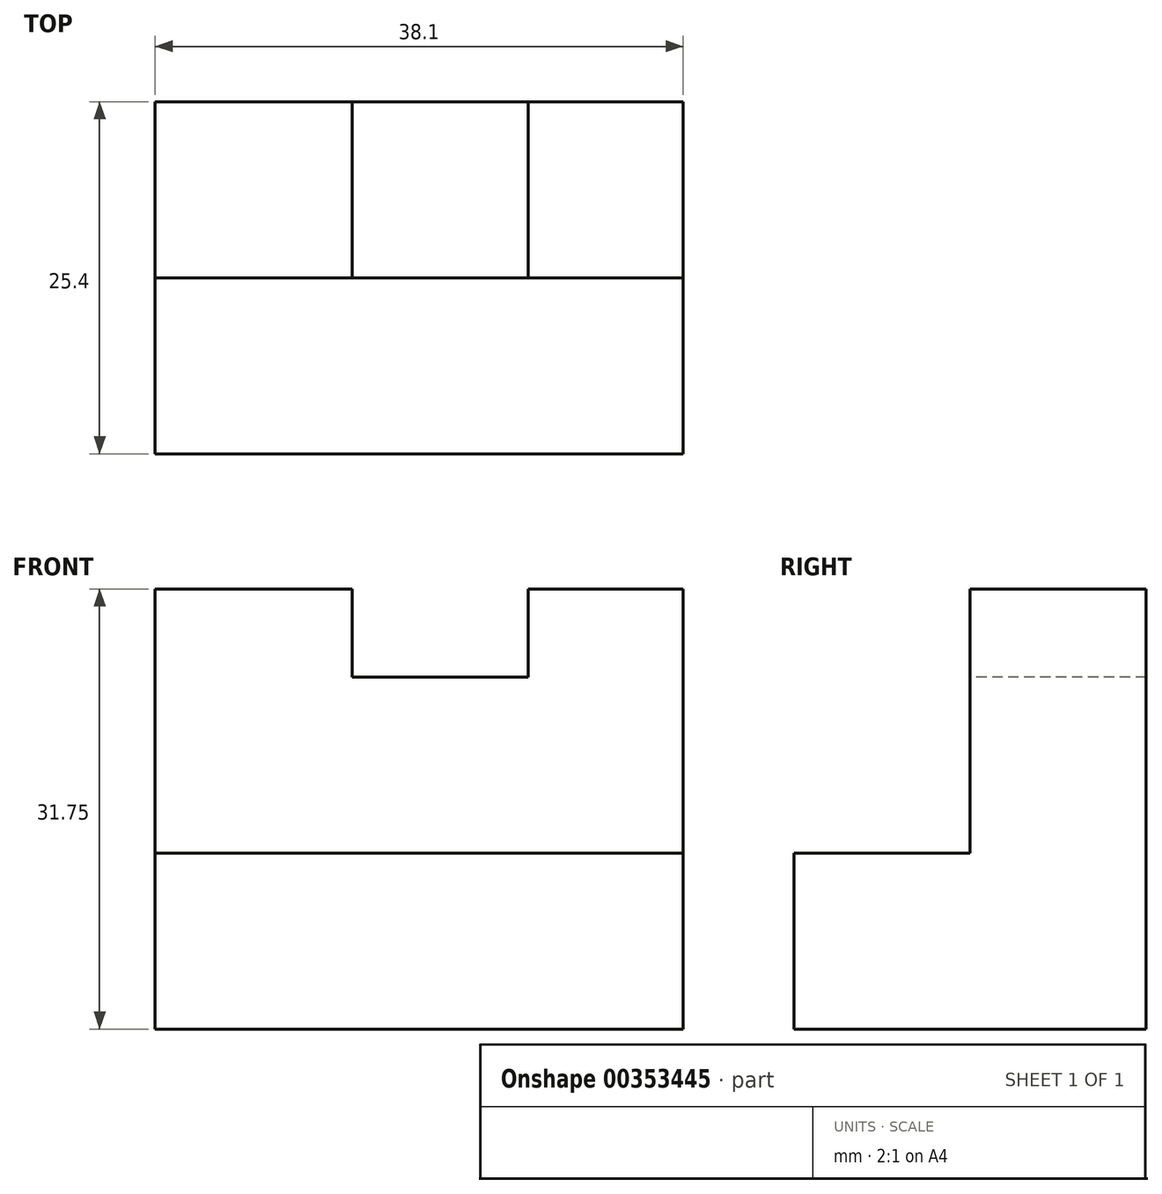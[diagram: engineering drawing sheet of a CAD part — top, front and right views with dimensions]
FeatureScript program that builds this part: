
annotation { "Feature Type Name" : "Feature", "Feature Type Description" : "" }
export const myFeature = defineFeature(function(context is Context, id is Id, definition is map)
    precondition{}
    {
        {
            var Q0;
            Q0=qCreatedBy(makeId("Right.planeOp"),FACE);
            var sketch = newSketch(context, id + "F0", { "sketchPlane" : qUnion([Q0])});
            skLineSegment(sketch, "E0", {"start": v(0, 0) * mm, "end": v(25.4, 0) * mm});
            skLineSegment(sketch, "E1", {"start": v(25.4, 31.75) * mm, "end": v(25.4, 0) * mm});
            skLineSegment(sketch, "E2", {"start": v(25.4, 31.75) * mm, "end": v(12.7, 31.75) * mm});
            skLineSegment(sketch, "E3", {"start": v(12.7, 31.75) * mm, "end": v(12.7, 12.7) * mm});
            skLineSegment(sketch, "E4", {"start": v(12.7, 12.7) * mm, "end": v(0, 12.7) * mm});
            skLineSegment(sketch, "E5", {"start": v(0, 12.7) * mm, "end": v(0, 0) * mm});
            skSolve(sketch);
        }
        {
            var Q0;
            Q0=makeQuery(id+"F0.imprint","IMPRINT",FACE,{"disambiguationData":[TD([[makeQuery(id+"F0.imprint","IMPRINT",EDGE,{"derivedFrom":sQuery(id+"F0.wireOp",EDGE,"E0")}),1.0]])]});
            extrude(context, id + "F1", {"entities" : qUnion([Q0]), "depth" : 38.1 * mm});
        }
        {
            var Q0;
            Q0=makeQuery(id+"F1.opExtrude","SWEPT_FACE",FACE,{"disambiguationData":[OSD([sQuery(id+"F0.wireOp",EDGE,"E2")])]});
            var sketch = newSketch(context, id + "F2", { "sketchPlane" : qUnion([Q0])});
            skLineSegment(sketch, "E6", {"start": v(14.21, 25.4) * mm, "end": v(14.21, 12.7) * mm});
            skLineSegment(sketch, "E7", {"start": v(14.21, 25.4) * mm, "end": v(26.91, 25.4) * mm});
            skLineSegment(sketch, "E8", {"start": v(26.91, 25.4) * mm, "end": v(26.91, 12.7) * mm});
            skLineSegment(sketch, "E9", {"start": v(26.91, 12.7) * mm, "end": v(14.21, 12.7) * mm});
            skSolve(sketch);
        }
        {
            var Q0;
            Q0 = qSketchRegion(id + "F2", true);
            extrude(context, id + "F3", {"entities" : qUnion([Q0]), "operationType" : NewBodyOperationType.REMOVE, "oppositeDirection" : true, "depth" : 6.35 * mm});
        }
    });
